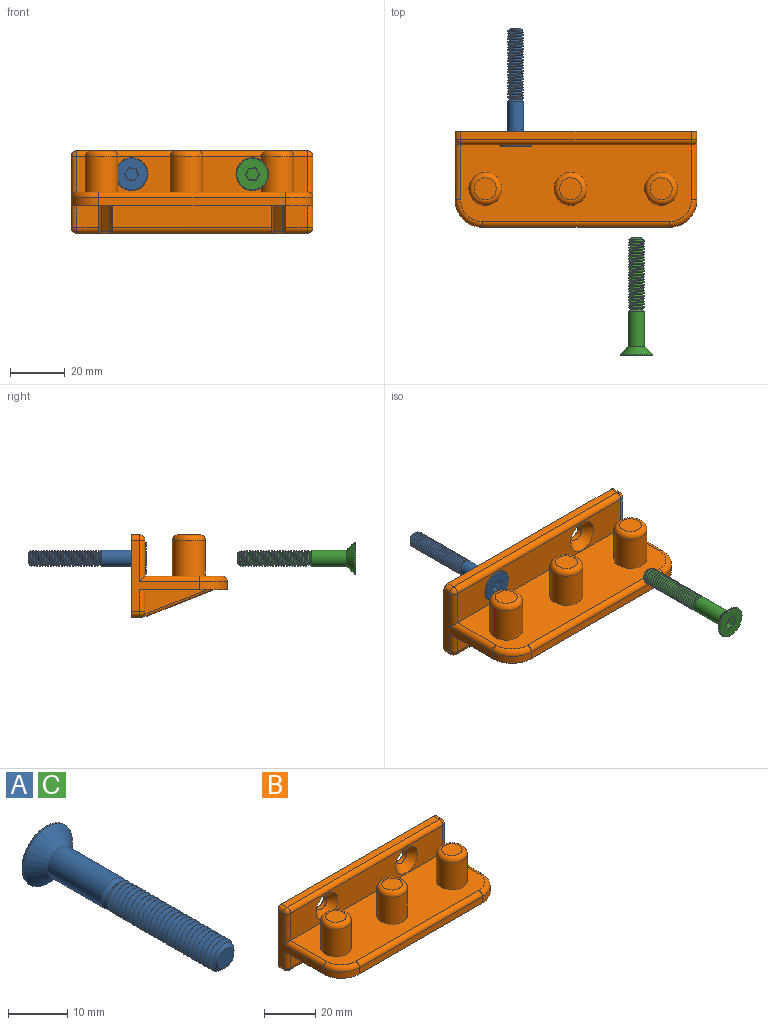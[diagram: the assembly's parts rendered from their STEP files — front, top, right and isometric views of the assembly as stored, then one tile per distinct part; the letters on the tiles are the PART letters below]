
ASSEMBLY  parts=3 mates=3
PART A: 26 faces, bbox 11.7x43.5x11.7 mm
  f0: cylinder r=2.97mm len=12.9mm, axis (0,1,0), area 240.5mm2, adj f3,f18
  f1: cylinder r=5.85mm len=11.7mm, axis (0,1,0), area 11mm2, adj f3,f17
  f2: plane 11.3x11.3mm, normal (0,1,0), area 82.8mm2, adj f11,f12,f13,f14,f15,f16,f17
  f3: cone r=2.85mm half-angle=45deg, axis (0,1,0), area 112.9mm2, adj f0,f1
  f4: plane 2.5x2.2mm, normal (0.93,0,-0.37), area 5.9mm2, adj f5,f9,f10,f11
  f5: plane 2.5x2.34mm, normal (0.15,0,-0.99), area 5.9mm2, adj f4,f6,f10,f12
  f6: plane 2.5x1.85mm, normal (-0.78,0,-0.62), area 5.9mm2, adj f5,f7,f10,f14
  f7: plane 2.5x2.2mm, normal (-0.93,0,0.37), area 5.9mm2, adj f6,f8,f10,f16
  f8: plane 2.5x2.34mm, normal (-0.15,0,0.99), area 5.9mm2, adj f7,f9,f10,f15
  f9: plane 2.5x1.85mm, normal (0.78,0,0.62), area 5.9mm2, adj f4,f8,f10,f13
  f10: plane 4.68x4.41mm, normal (0,1,0), area 14.6mm2, adj f4,f5,f6,f7,f8,f9
  f11: plane 2.42x1.09mm, normal (0.66,0.71,-0.26), area 0.7mm2, adj f2,f4,f12,f13
  f12: plane 2.57x0.57mm, normal (0.11,0.71,-0.7), area 0.7mm2, adj f2,f5,f11,f14
  f13: plane 2.07x1.7mm, normal (0.55,0.71,0.44), area 0.7mm2, adj f2,f9,f11,f15
  f14: plane 2.07x1.7mm, normal (-0.55,0.71,-0.44), area 0.7mm2, adj f2,f6,f12,f16
  f15: plane 2.57x0.57mm, normal (-0.11,0.71,0.7), area 0.7mm2, adj f2,f8,f13,f16
  f16: plane 2.42x1.09mm, normal (-0.66,0.71,0.26), area 0.7mm2, adj f2,f7,f14,f15
  f17: cone r=5.85mm half-angle=45deg, axis (0,-1,0), area 10.2mm2, adj f1,f2
  f18: cone r=2.28mm half-angle=43.9deg, axis (0,1,0), area 16.1mm2, adj f0,f19,f23,f24
  f19: cone r=3.15mm half-angle=47.8deg, axis (0,-1,0), area 6.7mm2, adj f18,f22,f23,f24,f25
  f20: plane 3.93x3.93mm, normal (0,-1,0), area 12.2mm2, adj f21
  f21: cone r=1.97mm half-angle=45deg, axis (0,1,0), area 12.6mm2, adj f20,f22,f23,f25
  f22: bspline ~26.64x6.85mm, area 385.1mm2, adj f19,f21,f23,f24,f25
  f23: bspline ~26.64x6.85mm, area 383mm2, adj f18,f19,f21,f22,f24,f25
  f24: plane 0.38x0.36mm, normal (0,0,1), area 0mm2, adj f18,f19,f22,f23
  f25: cylinder r=2.97mm len=24.38mm, axis (0,1,0), area 29.9mm2, adj f19,f21,f22,f23
PART B: 68 faces, bbox 89.6x35.8x30.1 mm
  f0: plane 22.48x8.79mm, normal (-1,0,0), area 99mm2, adj f6,f30,f50,f65,f66
  f1: plane 22.48x8.79mm, normal (1,0,0), area 99mm2, adj f5,f6,f53,f62,f63
  f2: plane 22.48x8.79mm, normal (1,0,0), area 99mm2, adj f4,f6,f49,f56,f57
  f3: plane 22.48x8.79mm, normal (-1,0,0), area 99mm2, adj f5,f6,f53,f59,f60
  f4: plane 8x7.95mm, normal (0,-1,0), area 63.6mm2, adj f2,f6,f34,f49
  f5: plane 58x7.95mm, normal (0,-1,0), area 461.3mm2, adj f1,f3,f6,f53
  f6: plane 88x32mm, normal (0,0,-1), area 2351.1mm2, adj f0,f1,f2,f3,f4,f5,f10,f11
  f7: cylinder r=2mm len=22mm, axis (0,-1,0), area 65.1mm2, adj f9,f10,f20,f37
  f8: cylinder r=2mm len=22mm, axis (0,1,0), area 65.1mm2, adj f9,f11,f18,f40
  f9: plane 84x28mm, normal (0,0,1), area 1985.2mm2, adj f7,f8,f15,f16,f18,f20,f21,f23
  f10: plane 25.95x25mm, normal (1,0,0), area 143.9mm2, adj f6,f7,f14,f19,f34,f36,f37,f47
  f11: plane 25.95x25mm, normal (-1,0,0), area 143.9mm2, adj f6,f8,f14,f17,f35,f40,f42,f51
  f12: plane 68x3mm, normal (0,-1,0), area 204mm2, adj f6,f16,f17,f19
  f13: plane 84x3mm, normal (0,0,1), area 252mm2, adj f14,f36,f39,f42
  f14: plane 88x29.95mm, normal (0,1,0), area 2576mm2, adj f10,f11,f13,f31,f36,f42,f43,f44
  f15: plane 84x13mm, normal (0,-1,0), area 865.8mm2, adj f9,f37,f39,f40,f45,f46
  f16: cylinder r=2mm len=68mm, axis (-1,0,0), area 213.6mm2, adj f9,f12,f18,f20
  f17: cylinder r=10mm len=10mm, axis (0,0,1), area 47.1mm2, adj f6,f11,f12,f18
  f18: torus R=8mm, axis (0,0,1), area 45.8mm2, adj f8,f9,f16,f17
  f19: cylinder r=10mm len=10mm, axis (0,0,-1), area 47.1mm2, adj f6,f10,f12,f20
  f20: torus R=8mm, axis (0,0,1), area 45.8mm2, adj f7,f9,f16,f19
  f21: cylinder r=6mm len=13mm, axis (0,0,-1), area 490.1mm2, adj f9,f29
  f22: plane 8x8mm, normal (0,0,1), area 50.3mm2, adj f29
  f23: cylinder r=6mm len=13mm, axis (0,0,-1), area 490.1mm2, adj f9,f28
  f24: plane 8x8mm, normal (0,0,1), area 50.3mm2, adj f28
  f25: cylinder r=6mm len=13mm, axis (0,0,-1), area 490.1mm2, adj f9,f27
  f26: plane 8x8mm, normal (0,0,1), area 50.3mm2, adj f27
  f27: torus R=4mm, axis (0,0,1), area 104.1mm2, adj f25,f26
  f28: torus R=4mm, axis (0,0,1), area 104.1mm2, adj f23,f24
  f29: torus R=4mm, axis (0,0,1), area 104.1mm2, adj f21,f22
  f30: plane 8x7.95mm, normal (0,-1,0), area 63.6mm2, adj f0,f6,f35,f50
  f31: plane 84x3.08mm, normal (0,0,-1), area 252.5mm2, adj f14,f47,f49,f50,f51,f53,f54,f55
  f32: plane 23.22x9.24mm, normal (0,-0.37,-0.93), area 75mm2, adj f6,f54,f56,f59
  f33: plane 23.22x9.24mm, normal (0,-0.37,-0.93), area 75mm2, adj f6,f55,f62,f65
  f34: cylinder r=2mm len=7.95mm, axis (0,0,1), area 25mm2, adj f4,f6,f10,f48
  f35: cylinder r=2mm len=7.95mm, axis (0,0,-1), area 25mm2, adj f6,f11,f30,f52
  f36: cylinder r=2mm len=3mm, axis (0,-1,0), area 9.4mm2, adj f10,f13,f14,f38
  f37: cylinder r=2mm len=15mm, axis (0,0,1), area 43.1mm2, adj f7,f10,f15,f38
  f38: sphere r=2mm, area 6.3mm2, adj f36,f37,f39
  f39: cylinder r=2mm len=84mm, axis (1,0,0), area 263.9mm2, adj f13,f15,f38,f41
  f40: cylinder r=2mm len=15mm, axis (0,0,-1), area 43.1mm2, adj f8,f11,f15,f41
  f41: sphere r=2mm, area 6.3mm2, adj f39,f40,f42
  f42: cylinder r=2mm len=3mm, axis (0,1,0), area 9.4mm2, adj f11,f13,f14,f41
  f43: cylinder r=3mm len=6mm, axis (0,-1,0), area 37.7mm2, adj f14,f45
  f44: cylinder r=3mm len=6mm, axis (0,-1,0), area 37.7mm2, adj f14,f46
  f45: cone r=3mm half-angle=45deg, axis (0,-1,0), area 120mm2, adj f15,f43
  f46: cone r=3mm half-angle=45deg, axis (0,-1,0), area 120mm2, adj f15,f44
  f47: cylinder r=2mm len=3mm, axis (0,1,0), area 9.4mm2, adj f10,f14,f31,f48
  f48: sphere r=2mm, area 6.3mm2, adj f34,f47,f49
  f49: cylinder r=2mm len=9mm, axis (-1,0,0), area 26mm2, adj f2,f4,f31,f48,f57,f58
  f50: cylinder r=2mm len=9mm, axis (-1,0,0), area 26mm2, adj f0,f30,f31,f52,f66,f67
  f51: cylinder r=2mm len=3mm, axis (0,-1,0), area 9.4mm2, adj f11,f14,f31,f52
  f52: sphere r=2mm, area 6.3mm2, adj f35,f50,f51
  f53: cylinder r=2mm len=60mm, axis (-1,0,0), area 183.9mm2, adj f1,f3,f5,f31,f60,f61,f63,f64
  f54: cylinder r=10mm len=3.7mm, axis (1,0,0), area 11.4mm2, adj f31,f32,f57,f60
  f55: cylinder r=10mm len=3.7mm, axis (1,0,0), area 11.4mm2, adj f31,f33,f63,f66
  f56: cylinder r=1mm len=23.59mm, axis (0,0.93,-0.37), area 37.8mm2, adj f2,f6,f32,f57
  f57: torus R=9mm, axis (-1,0,0), area 4.2mm2, adj f2,f49,f54,f56,f58
  f58: cylinder r=1mm len=0.08mm, axis (0,-1,0), area 0mm2, adj f31,f49,f57
  f59: cylinder r=1mm len=23.59mm, axis (0,-0.93,0.37), area 37.8mm2, adj f3,f6,f32,f60
  f60: torus R=9mm, axis (-1,0,0), area 4.2mm2, adj f3,f53,f54,f59,f61
  f61: cylinder r=1mm len=0.08mm, axis (0,-1,0), area 0mm2, adj f31,f53,f60
  f62: cylinder r=1mm len=23.59mm, axis (0,0.93,-0.37), area 37.8mm2, adj f1,f6,f33,f63
  f63: torus R=9mm, axis (-1,0,0), area 4.2mm2, adj f1,f53,f55,f62,f64
  f64: cylinder r=1mm len=0.08mm, axis (0,-1,0), area 0mm2, adj f31,f53,f63
  f65: cylinder r=1mm len=23.59mm, axis (0,-0.93,0.37), area 37.8mm2, adj f0,f6,f33,f66
  f66: torus R=9mm, axis (-1,0,0), area 4.2mm2, adj f0,f50,f55,f65,f67
  f67: cylinder r=1mm len=0.08mm, axis (0,-1,0), area 0mm2, adj f31,f50,f66
PART C: same geometry as A
PLACE A rot(axis=(1,0,0),180deg) t=(-11.12,9.21,9.29)mm
PLACE B t=(10.88,-5.29,-2.21)mm fixed
PLACE C rot(axis=(-0.43,0,-0.91),180deg) t=(32.88,-67.06,9.29)mm
MATE cylindrical C.f18 <-> B.f44  axis (0,-1,0) through (32.88,-67.06,9.29)mm
MATE cylindrical A.f0 <-> B.f43  axis (0,-1,0) through (-11.12,19.04,9.29)mm
MATE fastened B.f43 <-> A.f1  axis (0,-1,0) through (-11.12,9.71,9.29)mm
